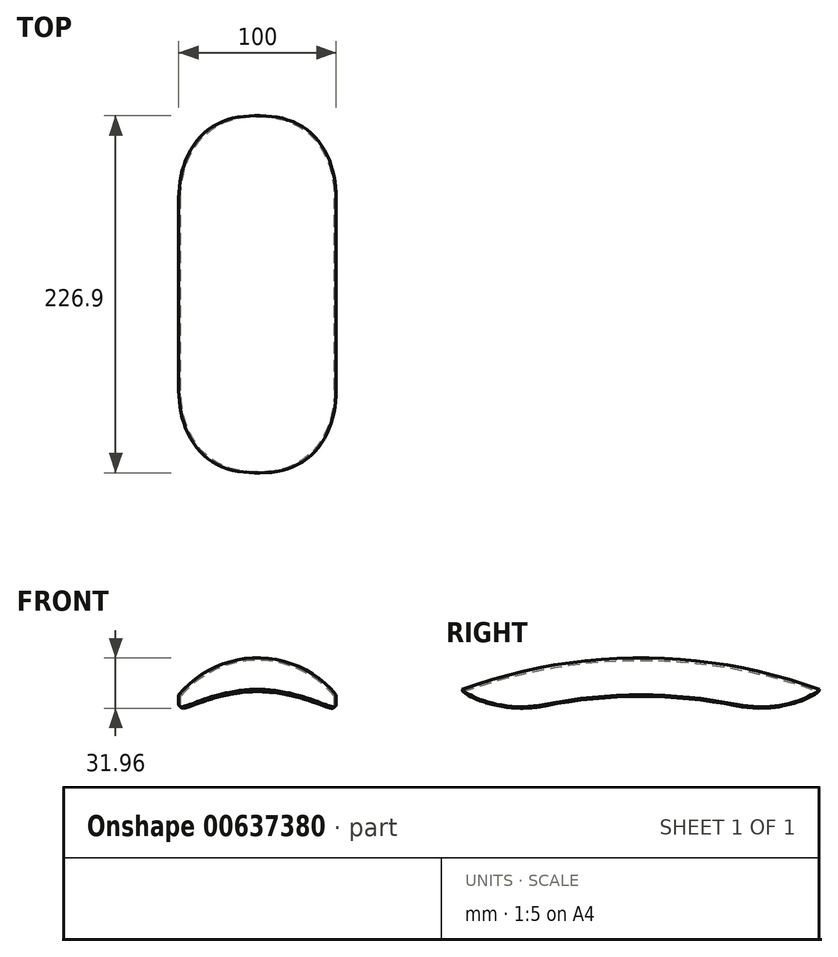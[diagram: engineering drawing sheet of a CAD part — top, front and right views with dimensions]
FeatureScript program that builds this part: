
annotation { "Feature Type Name" : "Feature", "Feature Type Description" : "" }
export const myFeature = defineFeature(function(context is Context, id is Id, definition is map)
    precondition{}
    {
        {
            var Q0;
            Q0=qCreatedBy(makeId("Front.planeOp"),FACE);
            var sketch = newSketch(context, id + "F0", { "sketchPlane" : qUnion([Q0])});
            skLineSegment(sketch, "E0", {"start": v(0, 0) * mm, "end": v(0, 266.7) * mm, "construction": true});
            skCircle(sketch, "E1", {"center": v(0, 266.7) * mm, "radius": 45 * mm, "construction": true});
            skArc(sketch, "E2", {"start": v(50, 308.23) * mm, "mid": v(0, 331.7) * mm, "end": v(-50, 308.23) * mm});
            skLineSegment(sketch, "E3", {"start": v(-50, 308.23) * mm, "end": v(50, 308.23) * mm, "construction": true});
            skArc(sketch, "E4.0", {"start": v(48.85, 307.27) * mm, "mid": v(0, 330.2) * mm, "end": v(-48.85, 307.27) * mm});
            skLineSegment(sketch, "E5", {"start": v(-48.85, 307.27) * mm, "end": v(-50, 308.23) * mm});
            skLineSegment(sketch, "E6", {"start": v(48.85, 307.27) * mm, "end": v(50, 308.23) * mm});
            skSolve(sketch);
        }
        {
            var Q0;
            Q0=qCreatedBy(makeId("Front.planeOp"),FACE);
            var sketch = newSketch(context, id + "F1", { "sketchPlane" : qUnion([Q0])});
            skLineSegment(sketch, "E7", {"start": v(0, 0) * mm, "end": v(170.88, 0) * mm, "construction": true});
            skSolve(sketch);
        }
        {
            var Q0;
            Q0=makeQuery(id+"F0.imprint","IMPRINT",FACE,{"disambiguationData":[TD([[makeQuery(id+"F0.imprint","IMPRINT",EDGE,{"derivedFrom":sQuery(id+"F0.wireOp",EDGE,"E2")}),1.0]])]});
            var Q1;
            Q1=sQuery(id+"F1.wireOp",EDGE,"E7");
            revolve(context, id + "F2", {"entities" : qUnion([Q0]), "axis" : qUnion([Q1]), "revolveType" : RevolveType.SYMMETRIC, "angle" : 40 * degree});
        }
        {
            var Q0;
            Q0=makeQuery(id+"F2.opRevolve","CAP_EDGE",EDGE,{"disambiguationData":[OSD([sQuery(id+"F0.wireOp",EDGE,"E6")])],"isStart":false});
            var Q1;
            Q1=makeQuery(id+"F2.opRevolve","CAP_EDGE",EDGE,{"disambiguationData":[OSD([sQuery(id+"F0.wireOp",EDGE,"E5")])],"isStart":false});
            var Q2;
            Q2=makeQuery(id+"F2.opRevolve","CAP_EDGE",EDGE,{"disambiguationData":[OSD([sQuery(id+"F0.wireOp",EDGE,"E6")])],"isStart":true});
            var Q3;
            Q3=makeQuery(id+"F2.opRevolve","CAP_EDGE",EDGE,{"disambiguationData":[OSD([sQuery(id+"F0.wireOp",EDGE,"E5")])],"isStart":true});
            fillet(context, id + "F3", {"entities" : qUnion([Q0, Q1, Q2, Q3]), "radius" : 52 * mm, "tangentPropagation" : true, "allowEdgeOverflow" : false});
        }
    });
